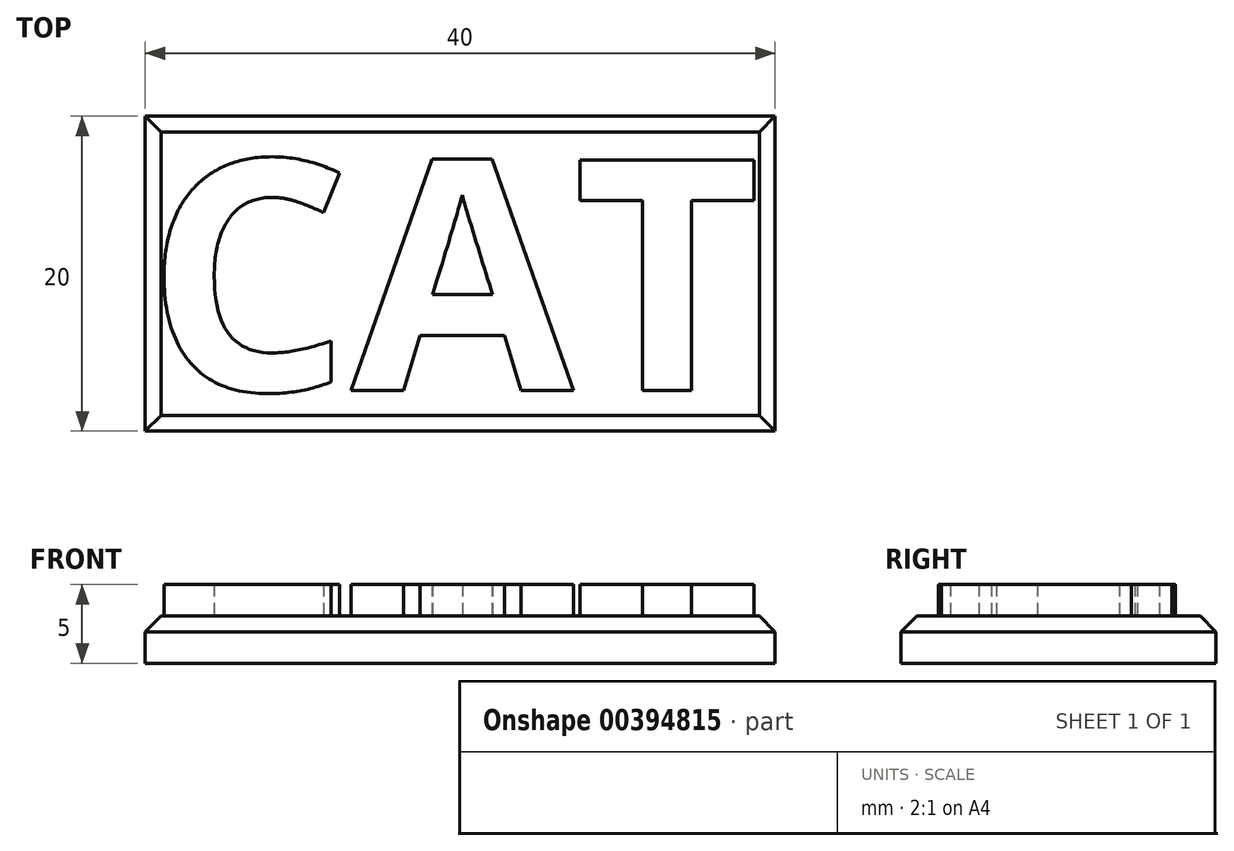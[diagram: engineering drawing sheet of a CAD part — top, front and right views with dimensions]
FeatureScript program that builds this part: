
annotation { "Feature Type Name" : "Feature", "Feature Type Description" : "" }
export const myFeature = defineFeature(function(context is Context, id is Id, definition is map)
    precondition{}
    {
        {
            var Q0;
            Q0=qCreatedBy(makeId("Top.planeOp"),FACE);
            var sketch = newSketch(context, id + "F0", { "sketchPlane" : qUnion([Q0])});
            skLineSegment(sketch, "E0.bottom", {"start": v(20, -10) * mm, "end": v(-20, -10) * mm});
            skLineSegment(sketch, "E0.top", {"start": v(20, 10) * mm, "end": v(-20, 10) * mm});
            skLineSegment(sketch, "E0.left", {"start": v(20, -10) * mm, "end": v(20, 10) * mm});
            skLineSegment(sketch, "E0.right", {"start": v(-20, -10) * mm, "end": v(-20, 10) * mm});
            skPoint(sketch, "E0.middle", {"position": v(0, 0) * mm});
            skSolve(sketch);
        }
        {
            var Q0;
            Q0=makeQuery(id+"F0.imprint","IMPRINT",FACE,{"disambiguationData":[TD([[makeQuery(id+"F0.imprint","IMPRINT",EDGE,{"derivedFrom":sQuery(id+"F0.wireOp",EDGE,"E0.bottom")}),-1.0]])]});
            extrude(context, id + "F1", {"entities" : qUnion([Q0]), "depth" : 3 * mm});
        }
        {
            var Q0;
            Q0=makeQuery(id+"F1.opExtrude","CAP_FACE",FACE,{"disambiguationData":[OSD([sQuery(id+"F0.wireOp",EDGE,"E0.bottom"),sQuery(id+"F0.wireOp",EDGE,"E0.top"),sQuery(id+"F0.wireOp",EDGE,"E0.left"),sQuery(id+"F0.wireOp",EDGE,"E0.right")])],"isStart":false});
            var sketch = newSketch(context, id + "F2", { "sketchPlane" : qUnion([Q0])});
            skText(sketch, "E1", { "text": "CAT", "fontName": "OpenSans-Bold.ttf"});
            const initialGuessF2  = {"E1": [-0.02, -0.00742, 1, 0, 0.01476]};
            skSetInitialGuess(sketch, initialGuessF2);
            skSolve(sketch);
        }
        {
            var Q0;
            Q0=makeQuery(id+"F2.imprint","IMPRINT",FACE,{"disambiguationData":[TD([[makeQuery(id+"F2.imprint","IMPRINT",EDGE,{"derivedFrom":sQuery(id+"F2.wireOp",EDGE,"E1.sketch_text.stroke-15")}),-1.0]])]});
            var Q1;
            Q1=makeQuery(id+"F2.imprint","IMPRINT",FACE,{"disambiguationData":[TD([[makeQuery(id+"F2.imprint","IMPRINT",EDGE,{"derivedFrom":sQuery(id+"F2.wireOp",EDGE,"E1.sketch_text.stroke-27")}),-1.0]])]});
            var Q2;
            Q2=makeQuery(id+"F2.imprint","IMPRINT",FACE,{"disambiguationData":[TD([[makeQuery(id+"F2.imprint","IMPRINT",EDGE,{"derivedFrom":sQuery(id+"F2.wireOp",EDGE,"E1.sketch_text.stroke-0")}),-1.0]])]});
            extrude(context, id + "F3", {"entities" : qUnion([Q0, Q1, Q2]), "operationType" : NewBodyOperationType.ADD, "depth" : 2 * mm});
        }
        {
            var Q0;
            Q0=makeQuery(id+"F1.opExtrude","CAP_EDGE",EDGE,{"disambiguationData":[OSD([sQuery(id+"F0.wireOp",EDGE,"E0.right")])],"isStart":false});
            var Q1;
            Q1=makeQuery(id+"F1.opExtrude","CAP_EDGE",EDGE,{"disambiguationData":[OSD([sQuery(id+"F0.wireOp",EDGE,"E0.bottom")])],"isStart":false});
            var Q2;
            Q2=makeQuery(id+"F1.opExtrude","CAP_EDGE",EDGE,{"disambiguationData":[OSD([sQuery(id+"F0.wireOp",EDGE,"E0.left")])],"isStart":false});
            var Q3;
            Q3=makeQuery(id+"F1.opExtrude","CAP_EDGE",EDGE,{"disambiguationData":[OSD([sQuery(id+"F0.wireOp",EDGE,"E0.top")])],"isStart":false});
            chamfer(context, id + "F4", {"entities" : qUnion([Q0, Q1, Q2, Q3]), "width" : 1 * mm, "tangentPropagation" : true});
        }
    });
